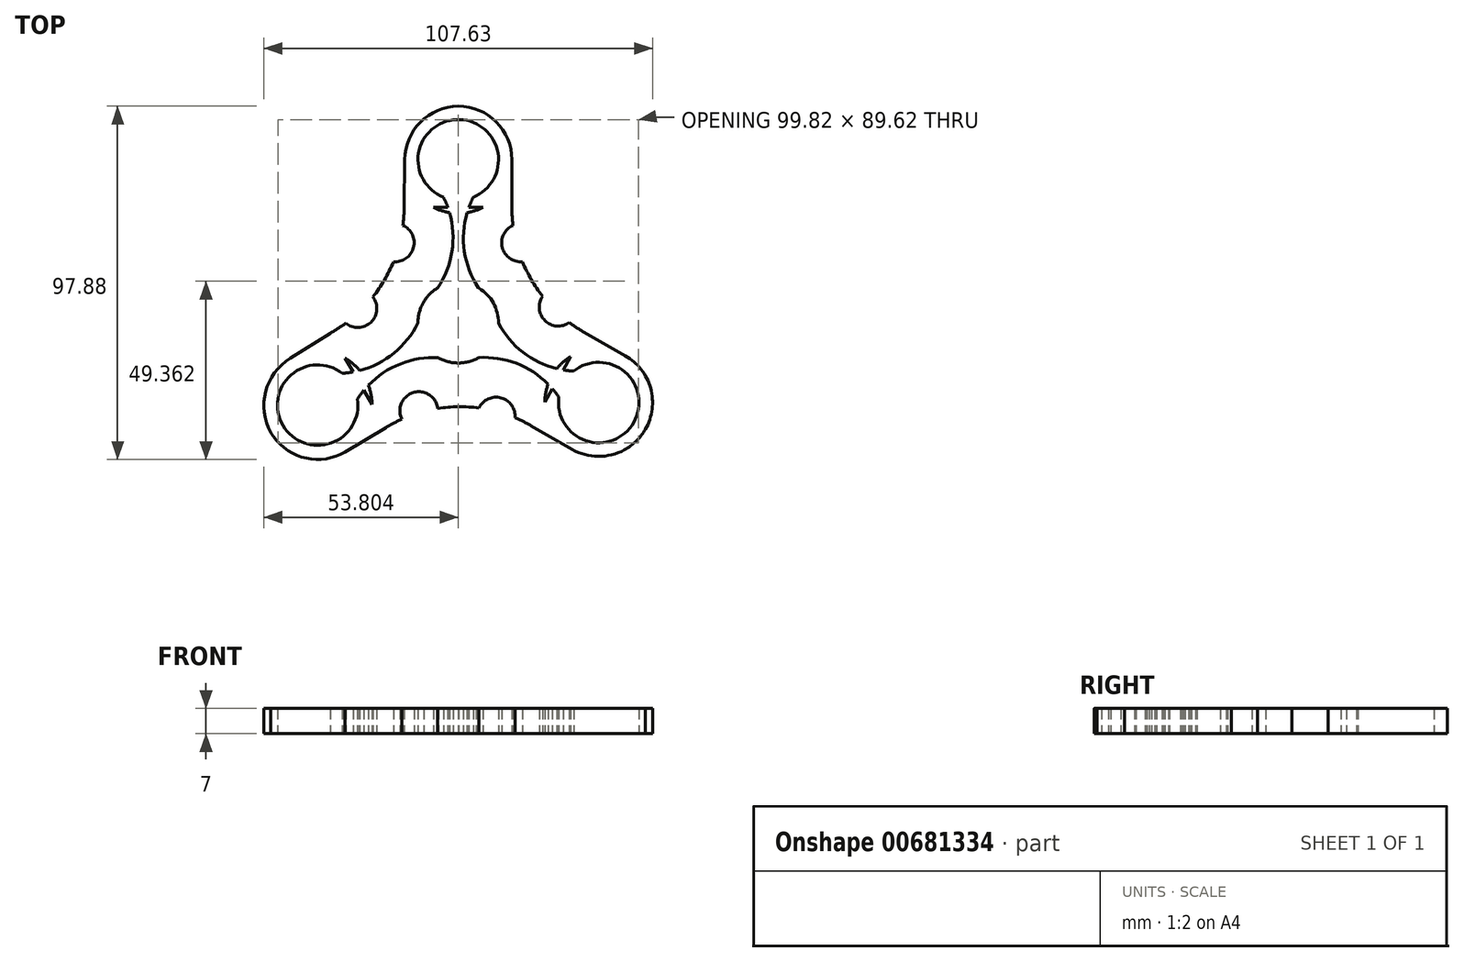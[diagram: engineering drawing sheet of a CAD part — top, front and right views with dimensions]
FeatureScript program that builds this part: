
annotation { "Feature Type Name" : "Feature", "Feature Type Description" : "" }
export const myFeature = defineFeature(function(context is Context, id is Id, definition is map)
    precondition{}
    {
        {
            var Q0;
            Q0=qCreatedBy(makeId("Top.planeOp"),FACE);
            var sketch = newSketch(context, id + "F0", { "sketchPlane" : qUnion([Q0])});
            skCircle(sketch, "E0", {"center": v(0, 0) * mm, "radius": 11.15 * mm});
            skPoint(sketch, "E1.0.midPoint", {"position": v(0, 17.25) * mm});
            skLineSegment(sketch, "E2", {"start": v(0, 0) * mm, "end": v(0, 60) * mm});
            skLineSegment(sketch, "E3", {"start": v(0, 0) * mm, "end": v(51.87, -29.49) * mm});
            skLineSegment(sketch, "E4", {"start": v(0, 0) * mm, "end": v(-51.92, -30.44) * mm});
            skCircle(sketch, "E5", {"center": v(0, 45.15) * mm, "radius": 14.85 * mm});
            skCircle(sketch, "E6", {"center": v(-38.93, -22.82) * mm, "radius": 15.06 * mm});
            skCircle(sketch, "E7", {"center": v(38.9, -22.12) * mm, "radius": 14.91 * mm});
            skLineSegment(sketch, "E8", {"start": v(0, 45.15) * mm, "end": v(-14.85, 45.15) * mm});
            skLineSegment(sketch, "E9", {"start": v(-14.85, 45.15) * mm, "end": v(14.85, 45.15) * mm});
            skLineSegment(sketch, "E10", {"start": v(-38.93, -22.82) * mm, "end": v(-46.54, -9.83) * mm});
            skLineSegment(sketch, "E11", {"start": v(-46.54, -9.83) * mm, "end": v(-31.31, -35.81) * mm});
            skLineSegment(sketch, "E12", {"start": v(38.9, -22.12) * mm, "end": v(46.27, -9.15) * mm});
            skLineSegment(sketch, "E13", {"start": v(46.27, -9.15) * mm, "end": v(31.54, -35.08) * mm});
            skCircle(sketch, "E14", {"center": v(0, 45.15) * mm, "radius": 11.15 * mm});
            skCircle(sketch, "E15", {"center": v(-38.93, -22.82) * mm, "radius": 11.15 * mm});
            skCircle(sketch, "E16", {"center": v(38.9, -22.12) * mm, "radius": 11.15 * mm});
            skLineSegment(sketch, "E17", {"start": v(0, 34) * mm, "end": v(0, 30) * mm});
            skLineSegment(sketch, "E18", {"start": v(-29.3, -17.18) * mm, "end": v(-25.94, -15.2) * mm});
            skLineSegment(sketch, "E19", {"start": v(29.21, -16.6) * mm, "end": v(25.94, -14.75) * mm});
            skLineSegment(sketch, "E20", {"start": v(27.58, -15.68) * mm, "end": v(20.25, -28.56) * mm});
            skLineSegment(sketch, "E21", {"start": v(27.58, -15.68) * mm, "end": v(34.95, -2.7) * mm});
            skLineSegment(sketch, "E22", {"start": v(-27.62, -16.2) * mm, "end": v(-35.43, -2.88) * mm});
            skLineSegment(sketch, "E23", {"start": v(-27.62, -16.2) * mm, "end": v(-20.08, -29.07) * mm});
            skLineSegment(sketch, "E24", {"start": v(0, 32) * mm, "end": v(-15, 32) * mm});
            skLineSegment(sketch, "E25", {"start": v(0, 32) * mm, "end": v(14.85, 32) * mm});
            skLineSegment(sketch, "E26", {"start": v(-35.43, -2.88) * mm, "end": v(-46.54, -9.83) * mm});
            skLineSegment(sketch, "E27", {"start": v(-20.08, -29.07) * mm, "end": v(-31.31, -35.81) * mm});
            skLineSegment(sketch, "E28", {"start": v(20.25, -28.56) * mm, "end": v(31.54, -35.08) * mm});
            skLineSegment(sketch, "E29", {"start": v(34.95, -2.7) * mm, "end": v(46.27, -9.15) * mm});
            skLineSegment(sketch, "E30", {"start": v(14.85, 45.15) * mm, "end": v(14.85, 32) * mm});
            skLineSegment(sketch, "E31", {"start": v(-14.85, 45.15) * mm, "end": v(-15, 32) * mm});
            skArc(sketch, "E32", {"start": v(14.85, 32) * mm, "mid": v(20.24, 11.95) * mm, "end": v(34.95, -2.7) * mm});
            skArc(sketch, "E33", {"start": v(-35.43, -2.88) * mm, "mid": v(-20.48, 11.79) * mm, "end": v(-15, 32) * mm});
            skArc(sketch, "E34", {"start": v(20.25, -28.56) * mm, "mid": v(0.02, -23.28) * mm, "end": v(-20.08, -29.07) * mm});
            skLineSegment(sketch, "E35", {"start": v(-20.48, 11.79) * mm, "end": v(-15, 32) * mm});
            skLineSegment(sketch, "E36", {"start": v(14.85, 32) * mm, "end": v(20.24, 11.95) * mm});
            skLineSegment(sketch, "E37", {"start": v(20.24, 11.95) * mm, "end": v(-20.48, 11.79) * mm});
            skLineSegment(sketch, "E38", {"start": v(-35.43, -2.88) * mm, "end": v(-20.48, 11.79) * mm});
            skLineSegment(sketch, "E39", {"start": v(-20.48, 11.79) * mm, "end": v(0, -23.5) * mm});
            skLineSegment(sketch, "E40", {"start": v(0, -23.5) * mm, "end": v(-20.08, -29.07) * mm});
            skLineSegment(sketch, "E41", {"start": v(0, -23.5) * mm, "end": v(20.24, 11.95) * mm});
            skLineSegment(sketch, "E42", {"start": v(34.95, -2.7) * mm, "end": v(20.24, 11.95) * mm});
            skLineSegment(sketch, "E43", {"start": v(0, -23.5) * mm, "end": v(20.25, -28.56) * mm});
            skLineSegment(sketch, "E44", {"start": v(10.13, -26.04) * mm, "end": v(27.6, 4.62) * mm});
            skLineSegment(sketch, "E45", {"start": v(-20.08, -29.07) * mm, "end": v(-10.04, -26.29) * mm});
            skLineSegment(sketch, "E46", {"start": v(-10.04, -26.29) * mm, "end": v(-27.96, 4.45) * mm});
            skLineSegment(sketch, "E47", {"start": v(-17.74, 21.9) * mm, "end": v(17.57, 21.9) * mm});
            skLineSegment(sketch, "E48", {"start": v(27.6, 4.62) * mm, "end": v(20.24, 11.95) * mm});
            skLineSegment(sketch, "E49", {"start": v(27.6, 4.62) * mm, "end": v(34.95, -2.7) * mm});
            skLineSegment(sketch, "E50", {"start": v(10.13, -26.04) * mm, "end": v(0, -23.5) * mm});
            skLineSegment(sketch, "E51", {"start": v(10.13, -26.04) * mm, "end": v(20.25, -28.56) * mm});
            skLineSegment(sketch, "E52", {"start": v(-10.04, -26.29) * mm, "end": v(-20.08, -29.07) * mm});
            skLineSegment(sketch, "E53", {"start": v(-10.04, -26.29) * mm, "end": v(0, -23.5) * mm});
            skLineSegment(sketch, "E54", {"start": v(-15, 32) * mm, "end": v(-17.74, 21.9) * mm});
            skLineSegment(sketch, "E55", {"start": v(-17.74, 21.9) * mm, "end": v(-20.48, 11.79) * mm});
            skLineSegment(sketch, "E56", {"start": v(14.85, 32) * mm, "end": v(17.57, 21.9) * mm});
            skLineSegment(sketch, "E57", {"start": v(20.24, 11.95) * mm, "end": v(17.57, 21.9) * mm});
            skLineSegment(sketch, "E58", {"start": v(-17.74, 21.9) * mm, "end": v(-15, 32) * mm});
            skLineSegment(sketch, "E59", {"start": v(-27.96, 4.45) * mm, "end": v(-20.48, 11.79) * mm});
            skLineSegment(sketch, "E60", {"start": v(-27.96, 4.45) * mm, "end": v(-35.43, -2.88) * mm});
            skLineSegment(sketch, "E61", {"start": v(-16.37, 26.95) * mm, "end": v(16.2, 26.95) * mm});
            skLineSegment(sketch, "E62", {"start": v(18.9, 16.92) * mm, "end": v(-19.1, 16.92) * mm});
            skLineSegment(sketch, "E63", {"start": v(23.92, 8.29) * mm, "end": v(5.08, -24.78) * mm});
            skLineSegment(sketch, "E64", {"start": v(31.28, 0.96) * mm, "end": v(15.19, -27.3) * mm});
            skLineSegment(sketch, "E65", {"start": v(-24.22, 8.12) * mm, "end": v(-5.02, -24.9) * mm});
            skLineSegment(sketch, "E66", {"start": v(-31.7, 0.78) * mm, "end": v(-15.06, -27.68) * mm});
            skArc(sketch, "E67", {"start": v(-5.68, -23.76) * mm, "mid": v(-12.4, -19.32) * mm, "end": v(-15.62, -26.72) * mm});
            skArc(sketch, "E68", {"start": v(-31.16, -0.12) * mm, "mid": v(-24.16, 0.16) * mm, "end": v(-23.66, 7.15) * mm});
            skArc(sketch, "E69", {"start": v(-17.95, 16.92) * mm, "mid": v(-12.39, 20.82) * mm, "end": v(-15.32, 26.95) * mm});
            skArc(sketch, "E70", {"start": v(15.17, 26.95) * mm, "mid": v(12.2, 20.8) * mm, "end": v(17.8, 16.92) * mm});
            skArc(sketch, "E71", {"start": v(15.74, -26.33) * mm, "mid": v(11.86, -20.82) * mm, "end": v(5.73, -23.62) * mm});
            skArc(sketch, "E72", {"start": v(23.37, 7.32) * mm, "mid": v(24, 0.58) * mm, "end": v(30.76, 0.06) * mm});
            skArc(sketch, "E73", {"start": v(0, 60) * mm, "mid": v(-10.45, 55.6) * mm, "end": v(-14.85, 45.15) * mm});
            skArc(sketch, "E74", {"start": v(14.85, 45.15) * mm, "mid": v(10.5, 55.65) * mm, "end": v(0, 60) * mm});
            skArc(sketch, "E75", {"start": v(51.87, -29.49) * mm, "mid": v(53.28, -18.16) * mm, "end": v(46.27, -9.15) * mm});
            skArc(sketch, "E76", {"start": v(31.54, -35.08) * mm, "mid": v(42.87, -36.53) * mm, "end": v(51.87, -29.49) * mm});
            skArc(sketch, "E77", {"start": v(-51.92, -30.44) * mm, "mid": v(-42.74, -37.45) * mm, "end": v(-31.31, -35.81) * mm});
            skArc(sketch, "E78", {"start": v(-46.54, -9.83) * mm, "mid": v(-53.33, -19.07) * mm, "end": v(-51.92, -30.44) * mm});
            skArc(sketch, "E79", {"start": v(-51.92, -30.44) * mm, "mid": v(-48.02, -34.84) * mm, "end": v(-42.74, -37.45) * mm});
            skArc(sketch, "E80", {"start": v(-53.33, -19.07) * mm, "mid": v(-53.75, -24.9) * mm, "end": v(-51.92, -30.44) * mm});
            skArc(sketch, "E81", {"start": v(42.87, -36.53) * mm, "mid": v(48.05, -33.88) * mm, "end": v(51.87, -29.49) * mm});
            skArc(sketch, "E82", {"start": v(51.87, -29.49) * mm, "mid": v(53.68, -23.96) * mm, "end": v(53.28, -18.16) * mm});
            skArc(sketch, "E83", {"start": v(0, 60) * mm, "mid": v(-5.67, 58.87) * mm, "end": v(-10.45, 55.6) * mm});
            skArc(sketch, "E84", {"start": v(10.5, 55.65) * mm, "mid": v(5.69, 58.88) * mm, "end": v(0, 60) * mm});
            skPoint(sketch, "E85.startSnap0", {"position": v(-53.75, -24.9) * mm});
            skArc(sketch, "E86", {"start": v(-0.12, 11.15) * mm, "mid": v(-9.7, 5.49) * mm, "end": v(-9.62, -5.64) * mm});
            skPoint(sketch, "E86.startSnap0", {"position": v(-0.12, 11.87) * mm});
            skArc(sketch, "E87", {"start": v(9.7, -5.51) * mm, "mid": v(9.3, 5.47) * mm, "end": v(-0.12, 11.15) * mm});
            skArc(sketch, "E88", {"start": v(-9.62, -5.64) * mm, "mid": v(0.07, -11.15) * mm, "end": v(9.7, -5.51) * mm});
            skArc(sketch, "E89", {"start": v(-9.7, 5.49) * mm, "mid": v(-11.18, -0.09) * mm, "end": v(-9.62, -5.64) * mm});
            skArc(sketch, "E90", {"start": v(-9.62, -5.64) * mm, "mid": v(-5.52, -9.71) * mm, "end": v(0.07, -11.15) * mm});
            skPoint(sketch, "E90.endSnap0", {"position": v(0.07, -11.15) * mm});
            skArc(sketch, "E91", {"start": v(0.07, -11.15) * mm, "mid": v(5.66, -9.66) * mm, "end": v(9.7, -5.51) * mm});
            skArc(sketch, "E92", {"start": v(9.7, -5.51) * mm, "mid": v(9.6, 5.65) * mm, "end": v(-0.12, 11.15) * mm});
            skArc(sketch, "E93", {"start": v(9.7, -5.51) * mm, "mid": v(11.08, -0.02) * mm, "end": v(9.7, 5.47) * mm});
            skPoint(sketch, "E93.endSnap0", {"position": v(9.3, 5.47) * mm});
            skArc(sketch, "E94", {"start": v(44.42, -12.42) * mm, "mid": v(35.97, -11.46) * mm, "end": v(29.21, -16.6) * mm});
            skArc(sketch, "E95", {"start": v(29.21, -16.6) * mm, "mid": v(28.3, -25.03) * mm, "end": v(33.4, -31.81) * mm});
            skArc(sketch, "E96", {"start": v(29.21, -16.6) * mm, "mid": v(27.93, -20.73) * mm, "end": v(28.3, -25.03) * mm});
            skArc(sketch, "E97", {"start": v(35.97, -11.36) * mm, "mid": v(32.15, -13.41) * mm, "end": v(29.21, -16.6) * mm});
            skPoint(sketch, "E97.startSnap0", {"position": v(35.97, -11.46) * mm});
            skArc(sketch, "E98", {"start": v(-29.3, -17.18) * mm, "mid": v(-36.18, -12.3) * mm, "end": v(-44.57, -13.2) * mm});
            skArc(sketch, "E99", {"start": v(-33.29, -32.44) * mm, "mid": v(-28.43, -25.56) * mm, "end": v(-29.3, -17.18) * mm});
            skArc(sketch, "E100", {"start": v(-28.43, -25.56) * mm, "mid": v(-28, -21.28) * mm, "end": v(-29.3, -17.18) * mm});
            skArc(sketch, "E101", {"start": v(-29.3, -17.18) * mm, "mid": v(-32.23, -14.01) * mm, "end": v(-36.18, -12.3) * mm});
            skArc(sketch, "E102", {"start": v(0, 34) * mm, "mid": v(7.78, 37.37) * mm, "end": v(11.15, 45.15) * mm});
            skArc(sketch, "E103", {"start": v(0, 34) * mm, "mid": v(4.26, 34.83) * mm, "end": v(7.78, 37.37) * mm});
            skArc(sketch, "E104", {"start": v(-11.15, 45.15) * mm, "mid": v(-7.7, 37.45) * mm, "end": v(0, 34) * mm});
            skArc(sketch, "E105", {"start": v(-7.7, 37.45) * mm, "mid": v(-4.2, 34.95) * mm, "end": v(0, 34) * mm});
            skArc(sketch, "E106", {"start": v(-32.23, -14.01) * mm, "mid": v(-19.82, -9.9) * mm, "end": v(-11.18, -0.09) * mm});
            skPoint(sketch, "E106.endSnap0", {"position": v(-11.18, -0.09) * mm});
            skArc(sketch, "E107", {"start": v(-5.52, -9.71) * mm, "mid": v(-18.33, -12.44) * mm, "end": v(-28, -21.28) * mm});
            skArc(sketch, "E108", {"start": v(27.93, -20.73) * mm, "mid": v(18.27, -12.23) * mm, "end": v(5.66, -9.66) * mm});
            skArc(sketch, "E109", {"start": v(11.08, -0.02) * mm, "mid": v(19.82, -9.53) * mm, "end": v(32.15, -13.41) * mm});
            skPoint(sketch, "E109.startSnap0", {"position": v(11.08, -0.02) * mm});
            skArc(sketch, "E110", {"start": v(-0.12, 11.15) * mm, "mid": v(-5.69, 9.63) * mm, "end": v(-9.7, 5.49) * mm});
            skArc(sketch, "E111", {"start": v(9.7, 5.47) * mm, "mid": v(5.57, 9.66) * mm, "end": v(-0.12, 11.15) * mm});
            skArc(sketch, "E112", {"start": v(-5.69, 9.63) * mm, "mid": v(-1.5, 22.1) * mm, "end": v(-4.2, 34.95) * mm});
            skArc(sketch, "E113", {"start": v(4.26, 34.97) * mm, "mid": v(1.47, 22.14) * mm, "end": v(5.57, 9.66) * mm});
            skPoint(sketch, "E113.startSnap0", {"position": v(4.26, 34.83) * mm});
            skSolve(sketch);
        }
        {
            var Q0;
            {var subQ6=sQuery(id+"F0.wireOp",EDGE,"E7");var subQ8=sQuery(id+"F0.wireOp",EDGE,"E81");var subQ9=makeQuery(id+"F0.imprint","INTERSECT",VERTEX,{"derivedFrom":[subQ6,subQ8]});Q0=makeQuery(id+"F0.imprint","IMPRINT",FACE,{"disambiguationData":[TD([[makeQuery(id+"F0.imprint","IMPRINT",EDGE,{"disambiguationData":[TD([[subQ9,1.0]])],"derivedFrom":subQ6}),1.0]])]});}
            var Q1;
            {var subQ4=sQuery(id+"F0.wireOp",EDGE,"E82");Q1=makeQuery(id+"F0.imprint","IMPRINT",FACE,{"disambiguationData":[TD([[makeQuery(id+"F0.imprint","IMPRINT",EDGE,{"derivedFrom":subQ4}),1.0]])]});}
            var Q2;
            {var subQ0=sQuery(id+"F0.wireOp",EDGE,"E16");var subQ1=makeQuery(id+"F0.imprint","INTERSECT",VERTEX,{"derivedFrom":[subQ0,sQuery(id+"F0.wireOp",EDGE,"E97")]});Q2=makeQuery(id+"F0.imprint","IMPRINT",FACE,{"disambiguationData":[TD([[makeQuery(id+"F0.imprint","IMPRINT",EDGE,{"disambiguationData":[TD([[subQ1,-1.0]])],"derivedFrom":subQ0}),-1.0]])]});}
            var Q3;
            {var subQ5=sQuery(id+"F0.wireOp",EDGE,"E7");var subQ7=makeQuery(id+"F0.imprint","INTERSECT",VERTEX,{"derivedFrom":[subQ5,sQuery(id+"F0.wireOp",EDGE,"E28")]});Q3=makeQuery(id+"F0.imprint","IMPRINT",FACE,{"disambiguationData":[TD([[makeQuery(id+"F0.imprint","IMPRINT",EDGE,{"disambiguationData":[TD([[subQ7,1.0]])],"derivedFrom":subQ5}),1.0]])]});}
            var Q4;
            {var subQ0=sQuery(id+"F0.wireOp",EDGE,"E28");Q4=makeQuery(id+"F0.imprint","IMPRINT",FACE,{"disambiguationData":[TD([[makeQuery(id+"F0.imprint","IMPRINT",EDGE,{"derivedFrom":subQ0}),1.0]])]});}
            var Q5;
            {var subQ3=sQuery(id+"F0.wireOp",EDGE,"E108");var subQ7=sQuery(id+"F0.wireOp",EDGE,"E7");var subQ9=makeQuery(id+"F0.imprint","INTERSECT",VERTEX,{"derivedFrom":[subQ7,subQ3]});Q5=makeQuery(id+"F0.imprint","IMPRINT",FACE,{"disambiguationData":[TD([[makeQuery(id+"F0.imprint","IMPRINT",EDGE,{"disambiguationData":[TD([[subQ9,-1.0]])],"derivedFrom":subQ7}),-1.0]])]});}
            var Q6;
            {var subQ0=sQuery(id+"F0.wireOp",EDGE,"E71");var subQ1=sQuery(id+"F0.wireOp",EDGE,"E44");var subQ2=makeQuery(id+"F0.imprint","INTERSECT",VERTEX,{"derivedFrom":[subQ1,subQ0]});Q6=makeQuery(id+"F0.imprint","IMPRINT",FACE,{"disambiguationData":[TD([[makeQuery(id+"F0.imprint","IMPRINT",EDGE,{"disambiguationData":[TD([[subQ2,-1.0]])],"derivedFrom":subQ1}),-1.0]])]});}
            var Q7;
            {var subQ0=sQuery(id+"F0.wireOp",EDGE,"E71");var subQ1=sQuery(id+"F0.wireOp",EDGE,"E44");var subQ2=makeQuery(id+"F0.imprint","INTERSECT",VERTEX,{"derivedFrom":[subQ1,subQ0]});Q7=makeQuery(id+"F0.imprint","IMPRINT",FACE,{"disambiguationData":[TD([[makeQuery(id+"F0.imprint","IMPRINT",EDGE,{"disambiguationData":[TD([[subQ2,-1.0]])],"derivedFrom":subQ1}),1.0]])]});}
            var Q8;
            {var subQ2=sQuery(id+"F0.wireOp",EDGE,"E34");var subQ7=sQuery(id+"F0.wireOp",EDGE,"E41");var subQ8=makeQuery(id+"F0.imprint","INTERSECT",VERTEX,{"derivedFrom":[subQ2,subQ7]});Q8=makeQuery(id+"F0.imprint","IMPRINT",FACE,{"disambiguationData":[TD([[makeQuery(id+"F0.imprint","IMPRINT",EDGE,{"disambiguationData":[TD([[subQ8,-1.0]])],"derivedFrom":subQ7}),-1.0]])]});}
            var Q9;
            {var subQ5=sQuery(id+"F0.wireOp",EDGE,"E41");var subQ6=sQuery(id+"F0.wireOp",EDGE,"E34");var subQ7=makeQuery(id+"F0.imprint","INTERSECT",VERTEX,{"derivedFrom":[subQ6,subQ5]});Q9=makeQuery(id+"F0.imprint","IMPRINT",FACE,{"disambiguationData":[TD([[makeQuery(id+"F0.imprint","IMPRINT",EDGE,{"disambiguationData":[TD([[subQ7,-1.0]])],"derivedFrom":subQ6}),-1.0]])]});}
            var Q10;
            {var subQ2=sQuery(id+"F0.wireOp",EDGE,"E34");var subQ7=sQuery(id+"F0.wireOp",EDGE,"E39");var subQ8=makeQuery(id+"F0.imprint","INTERSECT",VERTEX,{"derivedFrom":[subQ2,subQ7]});Q10=makeQuery(id+"F0.imprint","IMPRINT",FACE,{"disambiguationData":[TD([[makeQuery(id+"F0.imprint","IMPRINT",EDGE,{"disambiguationData":[TD([[subQ8,1.0]])],"derivedFrom":subQ7}),-1.0]])]});}
            var Q11;
            {var subQ0=sQuery(id+"F0.wireOp",EDGE,"E68");var subQ1=sQuery(id+"F0.wireOp",EDGE,"E65");var subQ2=makeQuery(id+"F0.imprint","INTERSECT",VERTEX,{"derivedFrom":[subQ1,subQ0]});Q11=makeQuery(id+"F0.imprint","IMPRINT",FACE,{"disambiguationData":[TD([[makeQuery(id+"F0.imprint","IMPRINT",EDGE,{"disambiguationData":[TD([[subQ2,-1.0]])],"derivedFrom":subQ1}),1.0]])]});}
            var Q12;
            {var subQ0=sQuery(id+"F0.wireOp",EDGE,"E106");var subQ1=sQuery(id+"F0.wireOp",EDGE,"E46");var subQ2=makeQuery(id+"F0.imprint","INTERSECT",VERTEX,{"derivedFrom":[subQ1,subQ0]});Q12=makeQuery(id+"F0.imprint","IMPRINT",FACE,{"disambiguationData":[TD([[makeQuery(id+"F0.imprint","IMPRINT",EDGE,{"disambiguationData":[TD([[subQ2,-1.0]])],"derivedFrom":subQ1}),-1.0]])]});}
            var Q13;
            {var subQ0=sQuery(id+"F0.wireOp",EDGE,"E106");var subQ1=sQuery(id+"F0.wireOp",EDGE,"E46");var subQ2=makeQuery(id+"F0.imprint","INTERSECT",VERTEX,{"derivedFrom":[subQ1,subQ0]});Q13=makeQuery(id+"F0.imprint","IMPRINT",FACE,{"disambiguationData":[TD([[makeQuery(id+"F0.imprint","IMPRINT",EDGE,{"disambiguationData":[TD([[subQ2,-1.0]])],"derivedFrom":subQ1}),1.0]])]});}
            var Q14;
            {var subQ5=sQuery(id+"F0.wireOp",EDGE,"E6");var subQ7=sQuery(id+"F0.wireOp",EDGE,"E106");var subQ8=makeQuery(id+"F0.imprint","INTERSECT",VERTEX,{"derivedFrom":[subQ5,subQ7]});Q14=makeQuery(id+"F0.imprint","IMPRINT",FACE,{"disambiguationData":[TD([[makeQuery(id+"F0.imprint","IMPRINT",EDGE,{"disambiguationData":[TD([[subQ8,-1.0]])],"derivedFrom":subQ5}),-1.0]])]});}
            var Q15;
            {var subQ3=sQuery(id+"F0.wireOp",EDGE,"E0");var subQ11=sQuery(id+"F0.wireOp",EDGE,"E110");var subQ12=makeQuery(id+"F0.imprint","INTERSECT",VERTEX,{"derivedFrom":[subQ3,subQ11]});Q15=makeQuery(id+"F0.imprint","IMPRINT",FACE,{"disambiguationData":[TD([[makeQuery(id+"F0.imprint","IMPRINT",EDGE,{"disambiguationData":[TD([[subQ12,-1.0]])],"derivedFrom":subQ3}),-1.0]])]});}
            var Q16;
            {var subQ1=sQuery(id+"F0.wireOp",EDGE,"E62");var subQ5=sQuery(id+"F0.wireOp",EDGE,"E112");var subQ6=makeQuery(id+"F0.imprint","INTERSECT",VERTEX,{"derivedFrom":[subQ1,subQ5]});Q16=makeQuery(id+"F0.imprint","IMPRINT",FACE,{"disambiguationData":[TD([[makeQuery(id+"F0.imprint","IMPRINT",EDGE,{"disambiguationData":[TD([[subQ6,-1.0]])],"derivedFrom":subQ1}),1.0]])]});}
            var Q17;
            {var subQ0=sQuery(id+"F0.wireOp",EDGE,"E69");var subQ1=sQuery(id+"F0.wireOp",EDGE,"E47");var subQ2=makeQuery(id+"F0.imprint","INTERSECT",VERTEX,{"derivedFrom":[subQ1,subQ0]});Q17=makeQuery(id+"F0.imprint","IMPRINT",FACE,{"disambiguationData":[TD([[makeQuery(id+"F0.imprint","IMPRINT",EDGE,{"disambiguationData":[TD([[subQ2,-1.0]])],"derivedFrom":subQ1}),-1.0]])]});}
            var Q18;
            {var subQ0=sQuery(id+"F0.wireOp",EDGE,"E69");var subQ1=sQuery(id+"F0.wireOp",EDGE,"E47");var subQ2=makeQuery(id+"F0.imprint","INTERSECT",VERTEX,{"derivedFrom":[subQ1,subQ0]});Q18=makeQuery(id+"F0.imprint","IMPRINT",FACE,{"disambiguationData":[TD([[makeQuery(id+"F0.imprint","IMPRINT",EDGE,{"disambiguationData":[TD([[subQ2,-1.0]])],"derivedFrom":subQ1}),1.0]])]});}
            var Q19;
            {var subQ5=sQuery(id+"F0.wireOp",EDGE,"E24");var subQ7=sQuery(id+"F0.wireOp",EDGE,"E5");var subQ8=makeQuery(id+"F0.imprint","INTERSECT",VERTEX,{"derivedFrom":[subQ7,subQ5]});Q19=makeQuery(id+"F0.imprint","IMPRINT",FACE,{"disambiguationData":[TD([[makeQuery(id+"F0.imprint","IMPRINT",EDGE,{"disambiguationData":[TD([[subQ8,-1.0]])],"derivedFrom":subQ7}),-1.0]])]});}
            var Q20;
            {var subQ0=sQuery(id+"F0.wireOp",EDGE,"E31");Q20=makeQuery(id+"F0.imprint","IMPRINT",FACE,{"disambiguationData":[TD([[makeQuery(id+"F0.imprint","IMPRINT",EDGE,{"derivedFrom":subQ0}),1.0]])]});}
            var Q21;
            {var subQ0=sQuery(id+"F0.wireOp",EDGE,"E24");var subQ1=sQuery(id+"F0.wireOp",EDGE,"E5");var subQ2=makeQuery(id+"F0.imprint","INTERSECT",VERTEX,{"derivedFrom":[subQ1,subQ0]});Q21=makeQuery(id+"F0.imprint","IMPRINT",FACE,{"disambiguationData":[TD([[makeQuery(id+"F0.imprint","IMPRINT",EDGE,{"disambiguationData":[TD([[subQ2,1.0]])],"derivedFrom":subQ0}),-1.0]])]});}
            var Q22;
            {var subQ3=sQuery(id+"F0.wireOp",EDGE,"E2");var subQ6=sQuery(id+"F0.wireOp",EDGE,"E14");var subQ9=makeQuery(id+"F0.imprint","INTERSECT",VERTEX,{"derivedFrom":[subQ3,subQ6]});Q22=makeQuery(id+"F0.imprint","IMPRINT",FACE,{"disambiguationData":[TD([[makeQuery(id+"F0.imprint","IMPRINT",EDGE,{"disambiguationData":[TD([[subQ9,-1.0]])],"derivedFrom":subQ6}),-1.0]])]});}
            var Q23;
            {var subQ7=sQuery(id+"F0.wireOp",EDGE,"E74");Q23=makeQuery(id+"F0.imprint","IMPRINT",FACE,{"disambiguationData":[TD([[makeQuery(id+"F0.imprint","IMPRINT",EDGE,{"derivedFrom":subQ7}),1.0]])]});}
            var Q24;
            {var subQ0=sQuery(id+"F0.wireOp",EDGE,"E30");Q24=makeQuery(id+"F0.imprint","IMPRINT",FACE,{"disambiguationData":[TD([[makeQuery(id+"F0.imprint","IMPRINT",EDGE,{"derivedFrom":subQ0}),-1.0]])]});}
            var Q25;
            {var subQ0=sQuery(id+"F0.wireOp",EDGE,"E25");var subQ1=sQuery(id+"F0.wireOp",EDGE,"E5");var subQ2=makeQuery(id+"F0.imprint","INTERSECT",VERTEX,{"derivedFrom":[subQ1,subQ0]});Q25=makeQuery(id+"F0.imprint","IMPRINT",FACE,{"disambiguationData":[TD([[makeQuery(id+"F0.imprint","IMPRINT",EDGE,{"disambiguationData":[TD([[subQ2,1.0]])],"derivedFrom":subQ0}),1.0]])]});}
            var Q26;
            {var subQ3=sQuery(id+"F0.wireOp",EDGE,"E113");var subQ7=sQuery(id+"F0.wireOp",EDGE,"E5");var subQ9=makeQuery(id+"F0.imprint","INTERSECT",VERTEX,{"derivedFrom":[subQ7,subQ3]});Q26=makeQuery(id+"F0.imprint","IMPRINT",FACE,{"disambiguationData":[TD([[makeQuery(id+"F0.imprint","IMPRINT",EDGE,{"disambiguationData":[TD([[subQ9,-1.0]])],"derivedFrom":subQ7}),-1.0]])]});}
            var Q27;
            {var subQ0=sQuery(id+"F0.wireOp",EDGE,"E113");var subQ1=sQuery(id+"F0.wireOp",EDGE,"E47");var subQ2=makeQuery(id+"F0.imprint","INTERSECT",VERTEX,{"derivedFrom":[subQ1,subQ0]});Q27=makeQuery(id+"F0.imprint","IMPRINT",FACE,{"disambiguationData":[TD([[makeQuery(id+"F0.imprint","IMPRINT",EDGE,{"disambiguationData":[TD([[subQ2,-1.0]])],"derivedFrom":subQ1}),1.0]])]});}
            var Q28;
            {var subQ0=sQuery(id+"F0.wireOp",EDGE,"E113");var subQ1=sQuery(id+"F0.wireOp",EDGE,"E47");var subQ2=makeQuery(id+"F0.imprint","INTERSECT",VERTEX,{"derivedFrom":[subQ1,subQ0]});Q28=makeQuery(id+"F0.imprint","IMPRINT",FACE,{"disambiguationData":[TD([[makeQuery(id+"F0.imprint","IMPRINT",EDGE,{"disambiguationData":[TD([[subQ2,-1.0]])],"derivedFrom":subQ1}),-1.0]])]});}
            var Q29;
            {var subQ0=sQuery(id+"F0.wireOp",EDGE,"E70");var subQ1=sQuery(id+"F0.wireOp",EDGE,"E62");var subQ4=makeQuery(id+"F0.imprint","INTERSECT",VERTEX,{"derivedFrom":[subQ1,subQ0]});Q29=makeQuery(id+"F0.imprint","IMPRINT",FACE,{"disambiguationData":[TD([[makeQuery(id+"F0.imprint","IMPRINT",EDGE,{"disambiguationData":[TD([[subQ4,-1.0]])],"derivedFrom":subQ1}),1.0]])]});}
            var Q30;
            {var subQ0=sQuery(id+"F0.wireOp",EDGE,"E29");Q30=makeQuery(id+"F0.imprint","IMPRINT",FACE,{"disambiguationData":[TD([[makeQuery(id+"F0.imprint","IMPRINT",EDGE,{"derivedFrom":subQ0}),-1.0]])]});}
            var Q31;
            {var subQ0=sQuery(id+"F0.wireOp",EDGE,"E109");var subQ1=sQuery(id+"F0.wireOp",EDGE,"E44");var subQ2=makeQuery(id+"F0.imprint","INTERSECT",VERTEX,{"derivedFrom":[subQ1,subQ0]});Q31=makeQuery(id+"F0.imprint","IMPRINT",FACE,{"disambiguationData":[TD([[makeQuery(id+"F0.imprint","IMPRINT",EDGE,{"disambiguationData":[TD([[subQ2,-1.0]])],"derivedFrom":subQ1}),-1.0]])]});}
            var Q32;
            {var subQ0=sQuery(id+"F0.wireOp",EDGE,"E109");var subQ1=sQuery(id+"F0.wireOp",EDGE,"E44");var subQ2=makeQuery(id+"F0.imprint","INTERSECT",VERTEX,{"derivedFrom":[subQ1,subQ0]});Q32=makeQuery(id+"F0.imprint","IMPRINT",FACE,{"disambiguationData":[TD([[makeQuery(id+"F0.imprint","IMPRINT",EDGE,{"disambiguationData":[TD([[subQ2,-1.0]])],"derivedFrom":subQ1}),1.0]])]});}
            var Q33;
            {var subQ0=sQuery(id+"F0.wireOp",EDGE,"E72");var subQ1=sQuery(id+"F0.wireOp",EDGE,"E63");var subQ2=makeQuery(id+"F0.imprint","INTERSECT",VERTEX,{"derivedFrom":[subQ1,subQ0]});Q33=makeQuery(id+"F0.imprint","IMPRINT",FACE,{"disambiguationData":[TD([[makeQuery(id+"F0.imprint","IMPRINT",EDGE,{"disambiguationData":[TD([[subQ2,-1.0]])],"derivedFrom":subQ1}),-1.0]])]});}
            var Q34;
            {var subQ1=sQuery(id+"F0.wireOp",EDGE,"E0");var subQ5=sQuery(id+"F0.wireOp",EDGE,"E111");var subQ6=makeQuery(id+"F0.imprint","INTERSECT",VERTEX,{"derivedFrom":[subQ1,subQ5]});Q34=makeQuery(id+"F0.imprint","IMPRINT",FACE,{"disambiguationData":[TD([[makeQuery(id+"F0.imprint","IMPRINT",EDGE,{"disambiguationData":[TD([[subQ6,1.0]])],"derivedFrom":subQ1}),-1.0]])]});}
            var Q35;
            {var subQ0=sQuery(id+"F0.wireOp",EDGE,"E27");var subQ2=sQuery(id+"F0.wireOp",EDGE,"E6");var subQ11=makeQuery(id+"F0.imprint","INTERSECT",VERTEX,{"derivedFrom":[subQ2,subQ0]});Q35=makeQuery(id+"F0.imprint","IMPRINT",FACE,{"disambiguationData":[TD([[makeQuery(id+"F0.imprint","IMPRINT",EDGE,{"disambiguationData":[TD([[subQ11,-1.0]])],"derivedFrom":subQ2}),1.0]])]});}
            var Q36;
            {var subQ0=sQuery(id+"F0.wireOp",EDGE,"E22");var subQ1=sQuery(id+"F0.wireOp",EDGE,"E6");var subQ2=makeQuery(id+"F0.imprint","INTERSECT",VERTEX,{"derivedFrom":[subQ1,subQ0]});Q36=makeQuery(id+"F0.imprint","IMPRINT",FACE,{"disambiguationData":[TD([[makeQuery(id+"F0.imprint","IMPRINT",EDGE,{"disambiguationData":[TD([[subQ2,1.0]])],"derivedFrom":subQ0}),1.0]])]});}
            var Q37;
            {var subQ0=sQuery(id+"F0.wireOp",EDGE,"E26");Q37=makeQuery(id+"F0.imprint","IMPRINT",FACE,{"disambiguationData":[TD([[makeQuery(id+"F0.imprint","IMPRINT",EDGE,{"derivedFrom":subQ0}),1.0]])]});}
            var Q38;
            {var subQ0=sQuery(id+"F0.wireOp",EDGE,"E27");var subQ1=sQuery(id+"F0.wireOp",EDGE,"E6");var subQ2=makeQuery(id+"F0.imprint","INTERSECT",VERTEX,{"derivedFrom":[subQ1,subQ0]});Q38=makeQuery(id+"F0.imprint","IMPRINT",FACE,{"disambiguationData":[TD([[makeQuery(id+"F0.imprint","IMPRINT",EDGE,{"disambiguationData":[TD([[subQ2,-1.0]])],"derivedFrom":subQ1}),-1.0]])]});}
            var Q39;
            {var subQ0=sQuery(id+"F0.wireOp",EDGE,"E67");var subQ1=sQuery(id+"F0.wireOp",EDGE,"E46");var subQ2=makeQuery(id+"F0.imprint","INTERSECT",VERTEX,{"derivedFrom":[subQ1,subQ0]});Q39=makeQuery(id+"F0.imprint","IMPRINT",FACE,{"disambiguationData":[TD([[makeQuery(id+"F0.imprint","IMPRINT",EDGE,{"disambiguationData":[TD([[subQ2,-1.0]])],"derivedFrom":subQ1}),-1.0]])]});}
            var Q40;
            {var subQ0=sQuery(id+"F0.wireOp",EDGE,"E67");var subQ1=sQuery(id+"F0.wireOp",EDGE,"E46");var subQ2=makeQuery(id+"F0.imprint","INTERSECT",VERTEX,{"derivedFrom":[subQ1,subQ0]});Q40=makeQuery(id+"F0.imprint","IMPRINT",FACE,{"disambiguationData":[TD([[makeQuery(id+"F0.imprint","IMPRINT",EDGE,{"disambiguationData":[TD([[subQ2,-1.0]])],"derivedFrom":subQ1}),1.0]])]});}
            var Q41;
            {var subQ5=sQuery(id+"F0.wireOp",EDGE,"E21");var subQ7=sQuery(id+"F0.wireOp",EDGE,"E7");var subQ8=makeQuery(id+"F0.imprint","INTERSECT",VERTEX,{"derivedFrom":[subQ7,subQ5]});Q41=makeQuery(id+"F0.imprint","IMPRINT",FACE,{"disambiguationData":[TD([[makeQuery(id+"F0.imprint","IMPRINT",EDGE,{"disambiguationData":[TD([[subQ8,-1.0]])],"derivedFrom":subQ7}),-1.0]])]});}
            var Q42;
            {var subQ4=sQuery(id+"F0.wireOp",EDGE,"E15");var subQ7=sQuery(id+"F0.wireOp",EDGE,"E4");var subQ9=makeQuery(id+"F0.imprint","INTERSECT",VERTEX,{"derivedFrom":[subQ7,subQ4]});Q42=makeQuery(id+"F0.imprint","IMPRINT",FACE,{"disambiguationData":[TD([[makeQuery(id+"F0.imprint","IMPRINT",EDGE,{"disambiguationData":[TD([[subQ9,-1.0]])],"derivedFrom":subQ4}),-1.0]])]});}
            var Q43;
            {var subQ6=sQuery(id+"F0.wireOp",EDGE,"E15");var subQ8=sQuery(id+"F0.wireOp",EDGE,"E4");var subQ9=makeQuery(id+"F0.imprint","INTERSECT",VERTEX,{"derivedFrom":[subQ8,subQ6]});Q43=makeQuery(id+"F0.imprint","IMPRINT",FACE,{"disambiguationData":[TD([[makeQuery(id+"F0.imprint","IMPRINT",EDGE,{"disambiguationData":[TD([[subQ9,1.0]])],"derivedFrom":subQ6}),-1.0]])]});}
            var Q44;
            {var subQ3=sQuery(id+"F0.wireOp",EDGE,"E107");var subQ7=sQuery(id+"F0.wireOp",EDGE,"E6");var subQ9=makeQuery(id+"F0.imprint","INTERSECT",VERTEX,{"derivedFrom":[subQ7,subQ3]});Q44=makeQuery(id+"F0.imprint","IMPRINT",FACE,{"disambiguationData":[TD([[makeQuery(id+"F0.imprint","IMPRINT",EDGE,{"disambiguationData":[TD([[subQ9,1.0]])],"derivedFrom":subQ7}),-1.0]])]});}
            extrude(context, id + "F1", {"entities" : qUnion([Q0, Q1, Q2, Q3, Q4, Q5, Q6, Q7, Q8, Q9, Q10, Q11, Q12, Q13, Q14, Q15, Q16, Q17, Q18, Q19, Q20, Q21, Q22, Q23, Q24, Q25, Q26, Q27, Q28, Q29, Q30, Q31, Q32, Q33, Q34, Q35, Q36, Q37, Q38, Q39, Q40, Q41, Q42, Q43, Q44]), "depth" : 7 * mm, "offsetDistance" : 25 * mm});
        }
    });
